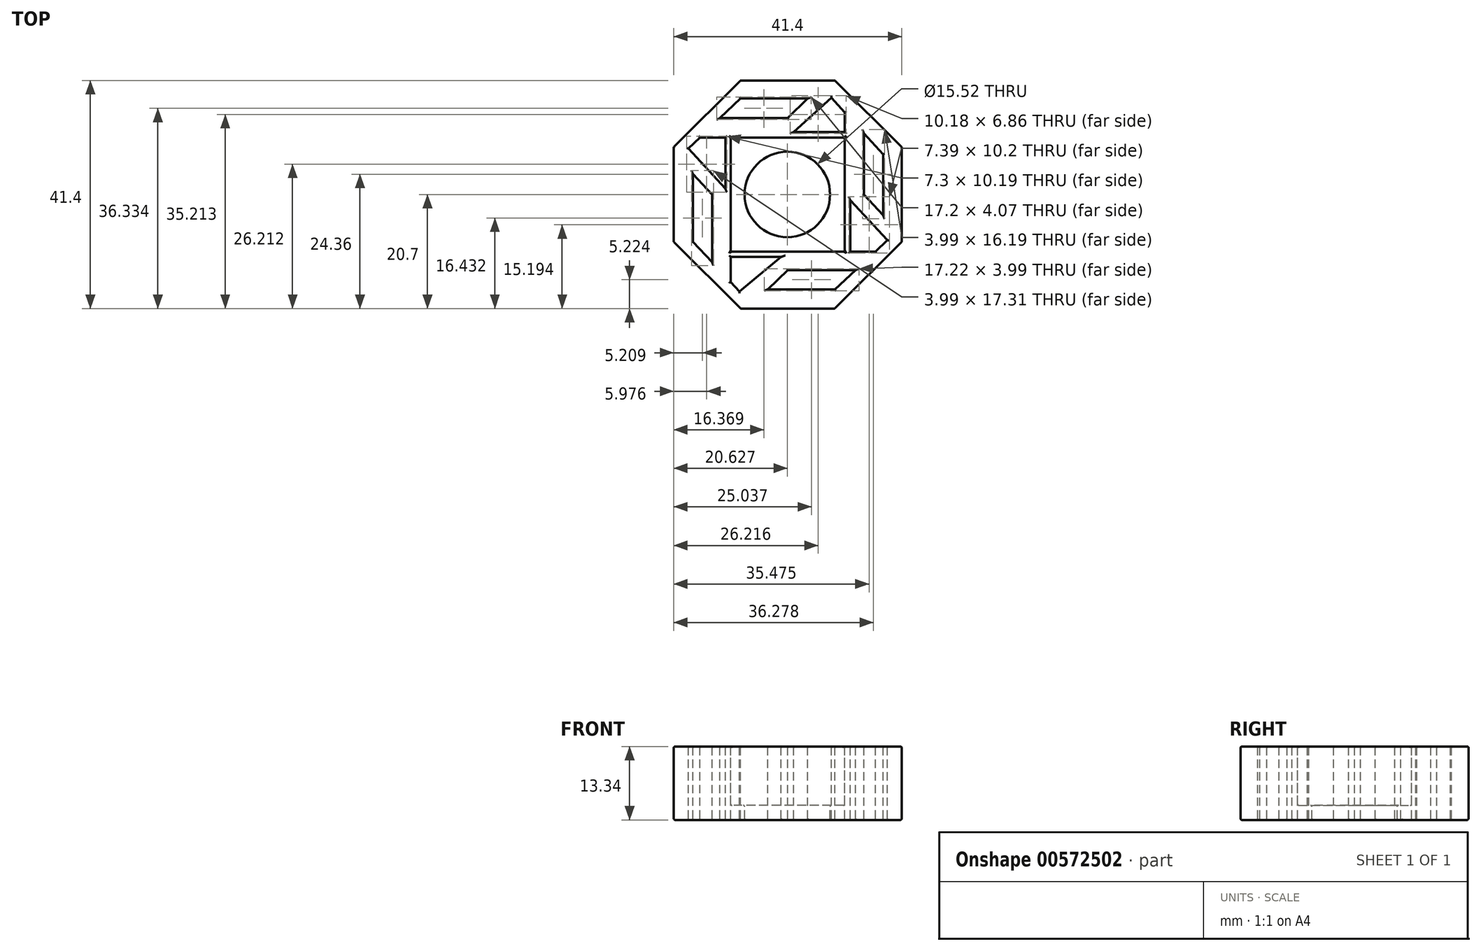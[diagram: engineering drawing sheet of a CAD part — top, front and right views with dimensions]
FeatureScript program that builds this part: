
annotation { "Feature Type Name" : "Feature", "Feature Type Description" : "" }
export const myFeature = defineFeature(function(context is Context, id is Id, definition is map)
    precondition{}
    {
        {
            var Q0;
            Q0=qCreatedBy(makeId("Top.planeOp"),FACE);
            var sketch = newSketch(context, id + "F0", { "sketchPlane" : qUnion([Q0])});
            skCircle(sketch, "E0.cCircle", {"center": v(20.7, 0) * mm, "radius": 20.7 * mm, "construction": true});
            skLineSegment(sketch, "E0.0", {"start": v(41.4, 8.57) * mm, "end": v(41.4, -8.57) * mm});
            skLineSegment(sketch, "E0.1", {"start": v(41.4, -8.57) * mm, "end": v(29.28, -20.7) * mm});
            skLineSegment(sketch, "E0.2", {"start": v(29.28, -20.7) * mm, "end": v(12.13, -20.7) * mm});
            skLineSegment(sketch, "E0.3", {"start": v(12.13, -20.7) * mm, "end": v(0, -8.57) * mm});
            skLineSegment(sketch, "E0.4", {"start": v(0, -8.57) * mm, "end": v(0, 8.57) * mm});
            skLineSegment(sketch, "E0.5", {"start": v(0, 8.57) * mm, "end": v(12.13, 20.7) * mm});
            skLineSegment(sketch, "E0.6", {"start": v(12.13, 20.7) * mm, "end": v(29.28, 20.7) * mm});
            skLineSegment(sketch, "E0.7", {"start": v(29.28, 20.7) * mm, "end": v(41.4, 8.57) * mm});
            skPoint(sketch, "E0.0.midPoint", {"position": v(41.4, 0) * mm});
            skPoint(sketch, "E1.orphan", {"position": v(0, 0) * mm});
            skSolve(sketch);
        }
        {
            var Q0;
            Q0 = qSketchRegion(id + "F0", true);
            extrude(context, id + "F1", {"entities" : qUnion([Q0]), "depth" : 13.33 * mm, "offsetDistance" : 25.4 * mm});
        }
        {
            var Q0;
            Q0=makeQuery(id+"F1.opExtrude","CAP_FACE",FACE,{"disambiguationData":[OSD([sQuery(id+"F0.wireOp",EDGE,"E0.0"),sQuery(id+"F0.wireOp",EDGE,"E0.1"),sQuery(id+"F0.wireOp",EDGE,"E0.2"),sQuery(id+"F0.wireOp",EDGE,"E0.3"),sQuery(id+"F0.wireOp",EDGE,"E0.4"),sQuery(id+"F0.wireOp",EDGE,"E0.5"),sQuery(id+"F0.wireOp",EDGE,"E0.6"),sQuery(id+"F0.wireOp",EDGE,"E0.7")])],"isStart":false});
            var sketch = newSketch(context, id + "F2", { "sketchPlane" : qUnion([Q0])});
            skCircle(sketch, "E2.cCircle", {"center": v(20.7, 0) * mm, "radius": 10.35 * mm, "construction": true});
            skLineSegment(sketch, "E2.0", {"start": v(10.35, -10.35) * mm, "end": v(10.35, 10.35) * mm});
            skLineSegment(sketch, "E2.1", {"start": v(10.35, 10.35) * mm, "end": v(31.05, 10.35) * mm});
            skLineSegment(sketch, "E2.2", {"start": v(31.05, 10.35) * mm, "end": v(31.05, -10.35) * mm});
            skLineSegment(sketch, "E2.3", {"start": v(31.05, -10.35) * mm, "end": v(10.35, -10.35) * mm});
            skPoint(sketch, "E2.0.midPoint", {"position": v(10.35, 0) * mm});
            skPoint(sketch, "E3.start.orphan", {"position": v(0, 0) * mm});
            skSolve(sketch);
        }
        {
            var Q0;
            Q0 = qSketchRegion(id + "F2", true);
            var Q1;
            Q1 = qSketchRegion(id + "F4", true);
            extrude(context, id + "F3", {"entities" : qUnion([Q0, Q1]), "operationType" : NewBodyOperationType.REMOVE, "oppositeDirection" : true, "depth" : 10.7 * mm, "offsetDistance" : 25.4 * mm});
        }
        {
            var Q0;
            Q0=makeQuery(id+"F3.boolean.opBoolean","COPY",FACE,{"derivedFrom":makeQuery(id+"F3.opExtrude","CAP_FACE",FACE,{"disambiguationData":[OSD([sQuery(id+"F2.wireOp",EDGE,"E2.0"),sQuery(id+"F2.wireOp",EDGE,"E2.1"),sQuery(id+"F2.wireOp",EDGE,"E2.2"),sQuery(id+"F2.wireOp",EDGE,"E2.3")])],"isStart":false})});
            var sketch = newSketch(context, id + "F4", { "sketchPlane" : qUnion([Q0])});
            skLineSegment(sketch, "E4", {"start": v(10.35, 0) * mm, "end": v(20.63, 0) * mm});
            skLineSegment(sketch, "E5", {"start": v(20.63, 0) * mm, "end": v(15.21, 0) * mm});
            skCircle(sketch, "E6", {"center": v(20.63, 0) * mm, "radius": 7.76 * mm});
            skSolve(sketch);
        }
        {
            var Q0;
            Q0=makeQuery(id+"F4.imprint","IMPRINT",FACE,{"disambiguationData":[TD([[makeQuery(id+"F4.imprint","IMPRINT",EDGE,{"derivedFrom":sQuery(id+"F4.wireOp",EDGE,"E6")}),1.0]])]});
            extrude(context, id + "F5", {"entities" : qUnion([Q0]), "operationType" : NewBodyOperationType.REMOVE, "oppositeDirection" : true, "depth" : 25.4 * mm, "offsetDistance" : 25.4 * mm});
        }
        {
            var Q0;
            Q0=makeQuery(id+"F1.opExtrude","CAP_FACE",FACE,{"disambiguationData":[OSD([sQuery(id+"F0.wireOp",EDGE,"E0.0"),sQuery(id+"F0.wireOp",EDGE,"E0.1"),sQuery(id+"F0.wireOp",EDGE,"E0.2"),sQuery(id+"F0.wireOp",EDGE,"E0.3"),sQuery(id+"F0.wireOp",EDGE,"E0.4"),sQuery(id+"F0.wireOp",EDGE,"E0.5"),sQuery(id+"F0.wireOp",EDGE,"E0.6"),sQuery(id+"F0.wireOp",EDGE,"E0.7")])],"isStart":false});
            var sketch = newSketch(context, id + "F6", { "sketchPlane" : qUnion([Q0])});
            skLineSegment(sketch, "E7", {"start": v(3.47, 0) * mm, "end": v(3.47, -8.57) * mm});
            skLineSegment(sketch, "E8", {"start": v(6.95, 0) * mm, "end": v(6.95, -12.28) * mm});
            skLineSegment(sketch, "E9", {"start": v(6.28, -11.57) * mm, "end": v(6.38, -11.47) * mm});
            skLineSegment(sketch, "E10", {"start": v(3.47, -8.57) * mm, "end": v(6.95, -12.28) * mm});
            skLineSegment(sketch, "E11", {"start": v(6.95, -12.28) * mm, "end": v(6.95, 0) * mm});
            skLineSegment(sketch, "E12", {"start": v(3.47, -8.57) * mm, "end": v(3.47, 3.74) * mm});
            skLineSegment(sketch, "E13", {"start": v(6.95, 0) * mm, "end": v(3.47, 3.74) * mm});
            skLineSegment(sketch, "E14", {"start": v(20.7, -13.74) * mm, "end": v(33, -13.74) * mm});
            skLineSegment(sketch, "E15", {"start": v(20.7, -17.22) * mm, "end": v(29.28, -17.22) * mm});
            skLineSegment(sketch, "E16", {"start": v(3.47, 0) * mm, "end": v(3.47, 3.74) * mm});
            skLineSegment(sketch, "E17", {"start": v(20.7, -17.22) * mm, "end": v(17.06, -17.22) * mm});
            skLineSegment(sketch, "E18", {"start": v(17.06, -17.22) * mm, "end": v(20.7, -13.74) * mm});
            skLineSegment(sketch, "E19", {"start": v(29.28, -17.22) * mm, "end": v(33, -13.74) * mm});
            skLineSegment(sketch, "E20", {"start": v(34.54, 0) * mm, "end": v(34.54, 11.1) * mm});
            skLineSegment(sketch, "E21", {"start": v(38.02, 0) * mm, "end": v(38.02, -3.78) * mm});
            skLineSegment(sketch, "E22", {"start": v(34.54, 0) * mm, "end": v(38.02, -3.78) * mm});
            skLineSegment(sketch, "E23", {"start": v(38.02, -3.78) * mm, "end": v(38.02, 7.3) * mm});
            skPoint(sketch, "E23.endSnap0", {"position": v(38.02, -1.9) * mm});
            skLineSegment(sketch, "E24", {"start": v(38.02, 7.3) * mm, "end": v(34.54, 11.1) * mm});
            skPoint(sketch, "E25.orphan", {"position": v(38.02, 8.57) * mm});
            skPoint(sketch, "E26.end.orphan", {"position": v(6.06, -14.64) * mm});
            skPoint(sketch, "E27.trimOffspring.end.orphan", {"position": v(10.35, 0) * mm});
            skPoint(sketch, "E28.end.orphan", {"position": v(20.7, -10.35) * mm});
            skPoint(sketch, "E29.start.orphan", {"position": v(20.7, -20.7) * mm});
            skPoint(sketch, "E30.end.orphan", {"position": v(35.34, -14.64) * mm});
            skPoint(sketch, "E31.orphan", {"position": v(41.4, 0) * mm});
            skPoint(sketch, "E32.start.orphan", {"position": v(31.05, 0) * mm});
            skPoint(sketch, "E33.end.orphan", {"position": v(35.34, 14.64) * mm});
            skLineSegment(sketch, "E34", {"start": v(17.06, -17.22) * mm, "end": v(20.7, -17.22) * mm});
            skLineSegment(sketch, "E35", {"start": v(20.7, 17.41) * mm, "end": v(24.34, 17.41) * mm});
            skLineSegment(sketch, "E36", {"start": v(17.06, -17.22) * mm, "end": v(29.28, -17.22) * mm});
            skLineSegment(sketch, "E37", {"start": v(24.34, 17.41) * mm, "end": v(12.13, 17.41) * mm});
            skLineSegment(sketch, "E38", {"start": v(20.7, 13.85) * mm, "end": v(24.34, 17.41) * mm});
            skLineSegment(sketch, "E39", {"start": v(20.7, 13.85) * mm, "end": v(8.4, 13.85) * mm});
            skLineSegment(sketch, "E40", {"start": v(8.4, 13.85) * mm, "end": v(12.13, 17.41) * mm});
            skPoint(sketch, "E41.end.orphan", {"position": v(6.06, 14.64) * mm});
            skPoint(sketch, "E42.start.orphan", {"position": v(20.7, 10.35) * mm});
            skPoint(sketch, "E43.start.orphan", {"position": v(20.7, 20.7) * mm});
            skSolve(sketch);
        }
        {
            var Q0;
            Q0 = qSketchRegion(id + "F6", true);
            extrude(context, id + "F7", {"entities" : qUnion([Q0]), "operationType" : NewBodyOperationType.REMOVE, "oppositeDirection" : true, "depth" : 25.4 * mm, "offsetDistance" : 25.4 * mm});
        }
        {
            var Q0;
            Q0=makeQuery(id+"F1.opExtrude","CAP_FACE",FACE,{"disambiguationData":[OSD([sQuery(id+"F0.wireOp",EDGE,"E0.0"),sQuery(id+"F0.wireOp",EDGE,"E0.1"),sQuery(id+"F0.wireOp",EDGE,"E0.2"),sQuery(id+"F0.wireOp",EDGE,"E0.3"),sQuery(id+"F0.wireOp",EDGE,"E0.4"),sQuery(id+"F0.wireOp",EDGE,"E0.5"),sQuery(id+"F0.wireOp",EDGE,"E0.6"),sQuery(id+"F0.wireOp",EDGE,"E0.7")])],"isStart":false});
            var sketch = newSketch(context, id + "F8", { "sketchPlane" : qUnion([Q0])});
            skLineSegment(sketch, "E44", {"start": v(4.74, 10.35) * mm, "end": v(9.37, 10.35) * mm});
            skLineSegment(sketch, "E45", {"start": v(4.74, 10.35) * mm, "end": v(3.47, 9.13) * mm});
            skLineSegment(sketch, "E46", {"start": v(3.47, 7.52) * mm, "end": v(9.37, 1.07) * mm});
            skLineSegment(sketch, "E47", {"start": v(9.37, 1.07) * mm, "end": v(2.68, 8.38) * mm});
            skLineSegment(sketch, "E48", {"start": v(2.68, 8.38) * mm, "end": v(3.47, 7.52) * mm});
            skLineSegment(sketch, "E49", {"start": v(3.47, 9.13) * mm, "end": v(4.74, 10.35) * mm});
            skLineSegment(sketch, "E50", {"start": v(4.74, 10.35) * mm, "end": v(2.68, 8.38) * mm});
            skPoint(sketch, "E51.orphan", {"position": v(3.47, 10.35) * mm});
            skPoint(sketch, "E52.orphan", {"position": v(10.35, 0) * mm});
            skLineSegment(sketch, "E53", {"start": v(9.37, 10.35) * mm, "end": v(9.37, 1.07) * mm});
            skLineSegment(sketch, "E54", {"start": v(9.37, 5.71) * mm, "end": v(10.35, 5.71) * mm});
            skLineSegment(sketch, "E55", {"start": v(10.35, -11.33) * mm, "end": v(10.35, -15.9) * mm});
            skLineSegment(sketch, "E56", {"start": v(10.35, -15.9) * mm, "end": v(10.35, -11.33) * mm});
            skLineSegment(sketch, "E57", {"start": v(10.35, -15.9) * mm, "end": v(11.95, -17.6) * mm});
            skLineSegment(sketch, "E58", {"start": v(11.95, -17.6) * mm, "end": v(10.35, -15.9) * mm});
            skLineSegment(sketch, "E59", {"start": v(19.52, -11.33) * mm, "end": v(11.95, -17.6) * mm});
            skLineSegment(sketch, "E60", {"start": v(14.86, -11.33) * mm, "end": v(19.52, -11.33) * mm});
            skLineSegment(sketch, "E61", {"start": v(19.52, -11.33) * mm, "end": v(10.35, -11.33) * mm});
            skPoint(sketch, "E62.orphan", {"position": v(14.86, -20.7) * mm});
            skPoint(sketch, "E63.end.orphan", {"position": v(20.7, -20.7) * mm});
            skPoint(sketch, "E64.orphan", {"position": v(20.7, -10.35) * mm});
            skPoint(sketch, "E65.start.orphan", {"position": v(14.86, -10.35) * mm});
            skLineSegment(sketch, "E66", {"start": v(36.63, -10.35) * mm, "end": v(38.81, -8.3) * mm});
            skLineSegment(sketch, "E67", {"start": v(32.03, -10.35) * mm, "end": v(36.63, -10.35) * mm});
            skLineSegment(sketch, "E68", {"start": v(32.03, -6.78) * mm, "end": v(32.03, -10.35) * mm});
            skLineSegment(sketch, "E69", {"start": v(32.03, -10.35) * mm, "end": v(32.03, -1.05) * mm});
            skPoint(sketch, "E70.end.orphan", {"position": v(41.4, 0) * mm});
            skPoint(sketch, "E71.orphan", {"position": v(31.05, 0) * mm});
            skLineSegment(sketch, "E72", {"start": v(32.03, -1.05) * mm, "end": v(38.81, -8.3) * mm});
            skLineSegment(sketch, "E73", {"start": v(31.05, 14.91) * mm, "end": v(28.6, 17.58) * mm});
            skLineSegment(sketch, "E74", {"start": v(31.05, 11.34) * mm, "end": v(31.05, 14.91) * mm});
            skLineSegment(sketch, "E75", {"start": v(25.53, 11.34) * mm, "end": v(21.78, 11.34) * mm});
            skLineSegment(sketch, "E76", {"start": v(21.78, 11.34) * mm, "end": v(31.05, 11.34) * mm});
            skPoint(sketch, "E77.end.orphan", {"position": v(20.7, 20.7) * mm});
            skPoint(sketch, "E78.orphan", {"position": v(20.7, 10.35) * mm});
            skLineSegment(sketch, "E79", {"start": v(21.78, 11.34) * mm, "end": v(28.6, 17.58) * mm});
            skSolve(sketch);
        }
        {
            var Q0;
            Q0 = qSketchRegion(id + "F8", true);
            extrude(context, id + "F9", {"entities" : qUnion([Q0]), "operationType" : NewBodyOperationType.REMOVE, "oppositeDirection" : true, "depth" : 25.4 * mm, "offsetDistance" : 25.4 * mm});
        }
        {
            var Q0;
            Q0 = qSketchRegion(id + "F8", true);
            extrude(context, id + "F10", {"entities" : qUnion([Q0]), "operationType" : NewBodyOperationType.REMOVE, "oppositeDirection" : true, "depth" : 25.4 * mm, "offsetDistance" : 25.4 * mm});
        }
        {
            var Q0;
            Q0=makeQuery(id+"F7.boolean.opBoolean","COPY",EDGE,{"derivedFrom":makeQuery(id+"F7.opExtrude","CAP_EDGE",EDGE,{"disambiguationData":[OSD([sQuery(id+"F6.wireOp",EDGE,"E37")])],"isStart":true})});
            var Q1;
            Q1=makeQuery(id+"F1.opExtrude","CAP_EDGE",EDGE,{"disambiguationData":[OSD([sQuery(id+"F0.wireOp",EDGE,"E0.6")])],"isStart":false});
            var Q2;
            Q2=makeQuery(id+"F1.opExtrude","CAP_EDGE",EDGE,{"disambiguationData":[OSD([sQuery(id+"F0.wireOp",EDGE,"E0.5")])],"isStart":false});
            var Q3;
            Q3=makeQuery(id+"F7.boolean.opBoolean","COPY",EDGE,{"derivedFrom":makeQuery(id+"F7.opExtrude","CAP_EDGE",EDGE,{"disambiguationData":[OSD([sQuery(id+"F6.wireOp",EDGE,"E40")])],"isStart":true})});
            var Q4;
            Q4=makeQuery(id+"F7.boolean.opBoolean","COPY",EDGE,{"derivedFrom":makeQuery(id+"F7.opExtrude","CAP_EDGE",EDGE,{"disambiguationData":[OSD([sQuery(id+"F6.wireOp",EDGE,"E39")])],"isStart":true})});
            var Q5;
            Q5=makeQuery(id+"F7.boolean.opBoolean","COPY",EDGE,{"derivedFrom":makeQuery(id+"F7.opExtrude","CAP_EDGE",EDGE,{"disambiguationData":[OSD([sQuery(id+"F6.wireOp",EDGE,"E38")])],"isStart":true})});
            var Q6;
            Q6=makeQuery(id+"F1.opExtrude","CAP_EDGE",EDGE,{"disambiguationData":[OSD([sQuery(id+"F0.wireOp",EDGE,"E0.7")])],"isStart":false});
            var Q7;
            Q7=makeQuery(id+"F9.boolean.opBoolean","COPY",EDGE,{"derivedFrom":makeQuery(id+"F9.opExtrude","CAP_EDGE",EDGE,{"disambiguationData":[OSD([sQuery(id+"F8.wireOp",EDGE,"E73")])],"isStart":true})});
            var Q8;
            Q8=makeQuery(id+"F9.boolean.opBoolean","COPY",EDGE,{"derivedFrom":makeQuery(id+"F9.opExtrude","CAP_EDGE",EDGE,{"disambiguationData":[OSD([sQuery(id+"F8.wireOp",EDGE,"E74")])],"isStart":true})});
            var Q9;
            Q9=makeQuery(id+"F9.boolean.opBoolean","COPY",EDGE,{"derivedFrom":makeQuery(id+"F9.opExtrude","CAP_EDGE",EDGE,{"disambiguationData":[OSD([sQuery(id+"F8.wireOp",EDGE,"E76")])],"isStart":true})});
            var Q10;
            Q10=makeQuery(id+"F9.boolean.opBoolean","COPY",EDGE,{"derivedFrom":makeQuery(id+"F9.opExtrude","CAP_EDGE",EDGE,{"disambiguationData":[OSD([sQuery(id+"F8.wireOp",EDGE,"E79")])],"isStart":true})});
            var Q11;
            Q11=makeQuery(id+"F3.boolean.opBoolean","COPY",EDGE,{"derivedFrom":makeQuery(id+"F3.opExtrude","CAP_EDGE",EDGE,{"disambiguationData":[OSD([sQuery(id+"F2.wireOp",EDGE,"E2.1")])],"isStart":true})});
            var Q12;
            Q12=makeQuery(id+"F3.boolean.opBoolean","COPY",EDGE,{"derivedFrom":makeQuery(id+"F3.opExtrude","CAP_EDGE",EDGE,{"disambiguationData":[OSD([sQuery(id+"F2.wireOp",EDGE,"E2.2")])],"isStart":true})});
            var Q13;
            Q13=makeQuery(id+"F1.opExtrude","CAP_FACE",FACE,{"disambiguationData":[OSD([sQuery(id+"F0.wireOp",EDGE,"E0.0"),sQuery(id+"F0.wireOp",EDGE,"E0.1"),sQuery(id+"F0.wireOp",EDGE,"E0.2"),sQuery(id+"F0.wireOp",EDGE,"E0.3"),sQuery(id+"F0.wireOp",EDGE,"E0.4"),sQuery(id+"F0.wireOp",EDGE,"E0.5"),sQuery(id+"F0.wireOp",EDGE,"E0.6"),sQuery(id+"F0.wireOp",EDGE,"E0.7")])],"isStart":false});
            var Q14;
            Q14=makeQuery(id+"F1.opExtrude","CAP_FACE",FACE,{"disambiguationData":[OSD([sQuery(id+"F0.wireOp",EDGE,"E0.0"),sQuery(id+"F0.wireOp",EDGE,"E0.1"),sQuery(id+"F0.wireOp",EDGE,"E0.2"),sQuery(id+"F0.wireOp",EDGE,"E0.3"),sQuery(id+"F0.wireOp",EDGE,"E0.4"),sQuery(id+"F0.wireOp",EDGE,"E0.5"),sQuery(id+"F0.wireOp",EDGE,"E0.6"),sQuery(id+"F0.wireOp",EDGE,"E0.7")])],"isStart":true});
            var Q15;
            Q15=makeQuery(id+"F1.opExtrude","SWEPT_FACE",FACE,{"disambiguationData":[OSD([sQuery(id+"F0.wireOp",EDGE,"E0.2")])]});
            var Q16;
            Q16=makeQuery(id+"F1.opExtrude","SWEPT_FACE",FACE,{"disambiguationData":[OSD([sQuery(id+"F0.wireOp",EDGE,"E0.1")])]});
            var Q17;
            Q17=makeQuery(id+"F1.opExtrude","SWEPT_FACE",FACE,{"disambiguationData":[OSD([sQuery(id+"F0.wireOp",EDGE,"E0.3")])]});
            var Q18;
            Q18=makeQuery(id+"F1.opExtrude","SWEPT_FACE",FACE,{"disambiguationData":[OSD([sQuery(id+"F0.wireOp",EDGE,"E0.4")])]});
            var Q19;
            Q19=makeQuery(id+"F1.opExtrude","SWEPT_FACE",FACE,{"disambiguationData":[OSD([sQuery(id+"F0.wireOp",EDGE,"E0.5")])]});
            var Q20;
            Q20=makeQuery(id+"F1.opExtrude","SWEPT_FACE",FACE,{"disambiguationData":[OSD([sQuery(id+"F0.wireOp",EDGE,"E0.6")])]});
            var Q21;
            Q21=makeQuery(id+"F1.opExtrude","SWEPT_FACE",FACE,{"disambiguationData":[OSD([sQuery(id+"F0.wireOp",EDGE,"E0.7")])]});
            fillet(context, id + "F11", {"entities" : qUnion([Q0, Q1, Q2, Q3, Q4, Q5, Q6, Q7, Q8, Q9, Q10, Q11, Q12, Q13, Q14, Q15, Q16, Q17, Q18, Q19, Q20, Q21]), "radius" : 0.25 * mm, "tangentPropagation" : true, "allowEdgeOverflow" : false});
        }
        {
            var Q0;
            Q0=makeQuery(id+"F3.boolean.opBoolean","COPY",FACE,{"derivedFrom":makeQuery(id+"F3.opExtrude","CAP_FACE",FACE,{"disambiguationData":[OSD([sQuery(id+"F2.wireOp",EDGE,"E2.0"),sQuery(id+"F2.wireOp",EDGE,"E2.1"),sQuery(id+"F2.wireOp",EDGE,"E2.2"),sQuery(id+"F2.wireOp",EDGE,"E2.3")])],"isStart":false})});
            var Q1;
            {var subQ0=makeQuery(id+"F5.opExtrude","SWEPT_FACE",FACE,{"disambiguationData":[OSD([sQuery(id+"F4.wireOp",EDGE,"IiZKSgw6-WM4C-81f6-uAzs-C4Q05lvn6M9K")])]});Q1=makeQuery(id+"F11.opFillet","BLEND_EDGE",EDGE,{"blendedFrom":[makeQuery(id+"F5.boolean.opBoolean","INTERSECT",EDGE,{"derivedFrom":[makeQuery(id+"F1.opExtrude","CAP_FACE",FACE,{"disambiguationData":[OSD([sQuery(id+"F0.wireOp",EDGE,"E0.0"),sQuery(id+"F0.wireOp",EDGE,"E0.1"),sQuery(id+"F0.wireOp",EDGE,"E0.2"),sQuery(id+"F0.wireOp",EDGE,"E0.3"),sQuery(id+"F0.wireOp",EDGE,"E0.4"),sQuery(id+"F0.wireOp",EDGE,"E0.5"),sQuery(id+"F0.wireOp",EDGE,"E0.6"),sQuery(id+"F0.wireOp",EDGE,"E0.7")])],"isStart":true}),subQ0]}),makeQuery(id+"F5.boolean.opBoolean","COPY",FACE,{"derivedFrom":subQ0})],"blendedInto":[makeQuery(id+"F5.boolean.opBoolean","COPY",FACE,{"derivedFrom":subQ0})]});}
            var Q2;
            Q2=makeQuery(id+"F3.boolean.opBoolean","COPY",FACE,{"derivedFrom":makeQuery(id+"F3.opExtrude","SWEPT_FACE",FACE,{"disambiguationData":[OSD([sQuery(id+"F2.wireOp",EDGE,"E2.0")])]})});
            var Q3;
            Q3=makeQuery(id+"F3.boolean.opBoolean","COPY",FACE,{"derivedFrom":makeQuery(id+"F3.opExtrude","SWEPT_FACE",FACE,{"disambiguationData":[OSD([sQuery(id+"F2.wireOp",EDGE,"E2.3")])]})});
            var Q4;
            Q4=makeQuery(id+"F3.boolean.opBoolean","COPY",FACE,{"derivedFrom":makeQuery(id+"F3.opExtrude","SWEPT_FACE",FACE,{"disambiguationData":[OSD([sQuery(id+"F2.wireOp",EDGE,"E2.2")])]})});
            var Q5;
            Q5=makeQuery(id+"F3.boolean.opBoolean","COPY",FACE,{"derivedFrom":makeQuery(id+"F3.opExtrude","SWEPT_FACE",FACE,{"disambiguationData":[OSD([sQuery(id+"F2.wireOp",EDGE,"E2.1")])]})});
            fillet(context, id + "F12", {"entities" : qUnion([Q0, Q1, Q2, Q3, Q4, Q5]), "radius" : 0.25 * mm, "tangentPropagation" : true, "allowEdgeOverflow" : false});
        }
    });
